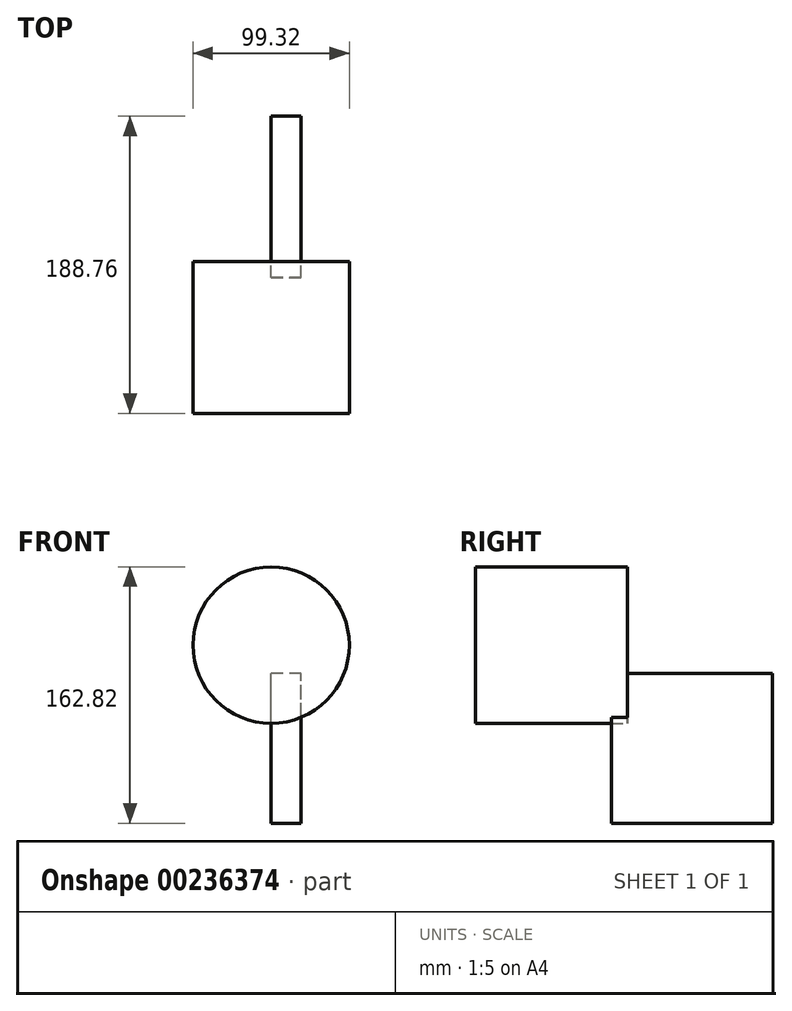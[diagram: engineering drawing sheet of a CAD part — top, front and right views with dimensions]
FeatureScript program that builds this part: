
annotation { "Feature Type Name" : "Feature", "Feature Type Description" : "" }
export const myFeature = defineFeature(function(context is Context, id is Id, definition is map)
    precondition{}
    {
        {
            var Q0;
            Q0=qCreatedBy(makeId("Front.planeOp"),FACE);
            var sketch = newSketch(context, id + "F0", { "sketchPlane" : qUnion([Q0])});
            skCircle(sketch, "E0", {"center": v(0, -1.14) * mm, "radius": 49.66 * mm});
            skSolve(sketch);
        }
        {
            var Q0;
            Q0=makeQuery(id+"F0.imprint","IMPRINT",FACE,{"disambiguationData":[TD([[makeQuery(id+"F0.imprint","IMPRINT",EDGE,{"derivedFrom":sQuery(id+"F0.wireOp",EDGE,"E0")}),1.0]])]});
            extrude(context, id + "F1", {"entities" : qUnion([Q0]), "depth" : 96.52 * mm});
        }
        {
            var Q0;
            Q0=qCreatedBy(makeId("Right.planeOp"),FACE);
            var sketch = newSketch(context, id + "F2", { "sketchPlane" : qUnion([Q0])});
            skLineSegment(sketch, "E1.bottom", {"start": v(-10.14, -114.3) * mm, "end": v(92.24, -114.3) * mm});
            skLineSegment(sketch, "E1.top", {"start": v(-10.14, -19.05) * mm, "end": v(92.24, -19.05) * mm});
            skLineSegment(sketch, "E1.left", {"start": v(-10.14, -114.3) * mm, "end": v(-10.14, -19.05) * mm});
            skLineSegment(sketch, "E1.right", {"start": v(92.24, -114.3) * mm, "end": v(92.24, -19.05) * mm});
            skSolve(sketch);
        }
        {
            var Q0;
            Q0=makeQuery(id+"F2.imprint","IMPRINT",FACE,{"disambiguationData":[TD([[makeQuery(id+"F2.imprint","IMPRINT",EDGE,{"derivedFrom":sQuery(id+"F2.wireOp",EDGE,"E1.bottom")}),1.0]])]});
            extrude(context, id + "F3", {"entities" : qUnion([Q0]), "operationType" : NewBodyOperationType.ADD, "depth" : 19.05 * mm});
        }
    });
